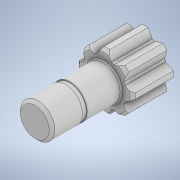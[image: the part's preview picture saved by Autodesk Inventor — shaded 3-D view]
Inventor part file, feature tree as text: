
AUTODESK INVENTOR PART (.ipt)
format: ipt  version: 2020 (Build 240168000, 168)  size: 339,456 bytes
history: native  units: mm
features: revolve x2, chamfer x2, sketch x2, plane x1, extrude x1, projected_geometry x1
ambient origin geometry x8: Origin, YZ Plane, XZ Plane, XY Plane, X Axis, Y Axis, Z Axis, Center Point
bodies: Solid1 (feature_tree)
feature tree (9):
  revolve  "Revolution1"  [1 undecoded]
  plane  "Work Plane1"
  revolve  "Revolution2"  Angle=90.0deg
  extrude  "Extrusion1"  Depth=3.0mm
  chamfer  "Chamfer1"  Distance=9.8mm
  chamfer  "Chamfer2"  Distance=7.6mm
  sketch  "Sketch1"  dims[d0=5.0mm d1=19.25mm]
  projected_geometry  "Projected Loop1"
  sketch  "Sketch3"  dims[d2=90.0deg d4=90.0deg d6=0.25mm d8=9.8mm d9=7.6mm d11=7.5mm d12=0.65mm d13=1.5708mm d14=0.32mm d19=80.0mm d21=360.0deg d23=35.0mm d24=0.0mm d26=0.5mm d27=2.0mm d28=45.0deg d29=30.0deg d30=-6.5mm d33=2.85mm d34=0.8mm d35=2.85mm d37=0.5mm d38=2.0mm d39=45.0deg d40=0.25mm d44=4.0mm d45=6.0mm d46=3.0mm]
note: 1 required parameter value undecoded (feature->parameter linkage not recoverable at this tier; creation-order binding heuristic only, values carry confidence <= 0.55)
